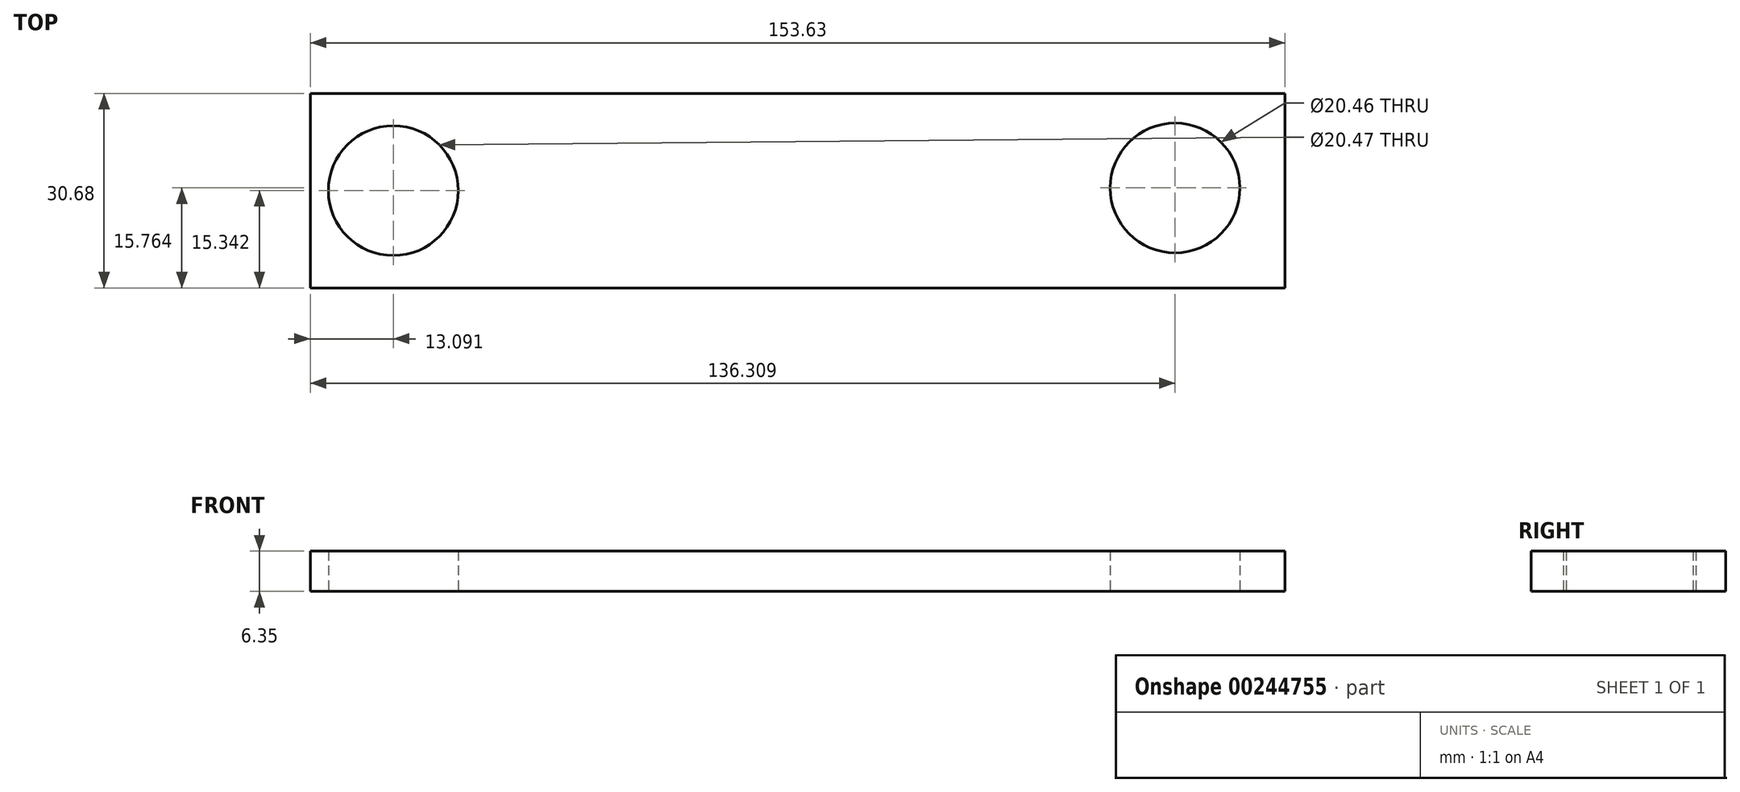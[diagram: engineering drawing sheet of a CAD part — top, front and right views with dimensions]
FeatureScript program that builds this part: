
annotation { "Feature Type Name" : "Feature", "Feature Type Description" : "" }
export const myFeature = defineFeature(function(context is Context, id is Id, definition is map)
    precondition{}
    {
        {
            var Q0;
            Q0=qCreatedBy(makeId("Top.planeOp"),FACE);
            var sketch = newSketch(context, id + "F0", { "sketchPlane" : qUnion([Q0])});
            skLineSegment(sketch, "E0.bottom", {"start": v(-28.76, 5.88) * mm, "end": v(124.87, 5.88) * mm});
            skLineSegment(sketch, "E0.top", {"start": v(-28.76, -24.8) * mm, "end": v(124.87, -24.8) * mm});
            skLineSegment(sketch, "E0.left", {"start": v(-28.76, 5.88) * mm, "end": v(-28.76, -24.8) * mm});
            skLineSegment(sketch, "E0.right", {"start": v(124.87, 5.88) * mm, "end": v(124.87, -24.8) * mm});
            skSolve(sketch);
        }
        {
            var Q0;
            Q0=makeQuery(id+"F0.imprint","IMPRINT",FACE,{"disambiguationData":[TD([[makeQuery(id+"F0.imprint","IMPRINT",EDGE,{"derivedFrom":sQuery(id+"F0.wireOp",EDGE,"E0.bottom")}),-1.0]])]});
            extrude(context, id + "F1", {"entities" : qUnion([Q0]), "depth" : 6.35 * mm});
        }
        {
            var Q0;
            Q0=qCreatedBy(makeId("Top.planeOp"),FACE);
            var sketch = newSketch(context, id + "F2", { "sketchPlane" : qUnion([Q0])});
            skCircle(sketch, "E1", {"center": v(-15.67, -9.46) * mm, "radius": 10.24 * mm});
            skCircle(sketch, "E2", {"center": v(107.55, -9.04) * mm, "radius": 10.23 * mm});
            skSolve(sketch);
        }
        {
            var Q0;
            Q0 = qSketchRegion(id + "F2", true);
            extrude(context, id + "F3", {"entities" : qUnion([Q0]), "operationType" : NewBodyOperationType.REMOVE, "depth" : 25.4 * mm});
        }
    });
